# Revit family: Heater-Bromic-Eclipse-Electric-Portable_EU
name_source: partatom
category: Mechanical Equipment
units: mm (PartAtom-declared; Revit-internal decimal feet)

## family parameters
Always vertical = No
Classification = None
Cut with Voids When Loaded = No
OmniClass Number = 23.75.10.14
OmniClass Title = Independent Electric Heating Units
Part Type = Normal
Room Calculation Point = No
Round Connector Dimension = Use Diameter
Shared = No
Work Plane-Based = Yes

## types (1)
- Eclipse Electric - Portable
    Apparent Load = 3000 VA
    Approximate Heat Area = 11.00 m²
    Default Elevation = 0 mm  [stored 0 ft]
    Depth = 2286 mm  [stored 7.5 ft]
    Description = The Eclipse Smart-Heat Portable provides the ideal solution for flexible heating needs. With it’s minimalist yet striking portable design, enjoy heat and dimmable LED light wherever it’s required.
    Diameter = 711 mm
    Frequency = 60 Hz
    Height = 2388 mm
    Load Classification = Other
    Load Sub-Classification Motor = No
    Manufacturer = Bromic Heating
    Material = Metal-Steel-Bromic-Black
    Model = Eclipse Smart-Heat™ Electric Portable
    Number of Poles = 1
    Power Factor = 1
    Product data url = https://www.bimobject.com
    ProductCode = BH0820011
    URL = https://www.bromic.co.uk
    Utility = No
    Voltage = 240 V
    Wattage = 3000 W
    Width = 610 mm

note: [stored X ft] marks values corroborated as IEEE doubles in the binary element streams (Revit-internal decimal feet)

## geometry (parser evidence)
native form markers: Sweep x4
no freeform markers — native parametric forms only
